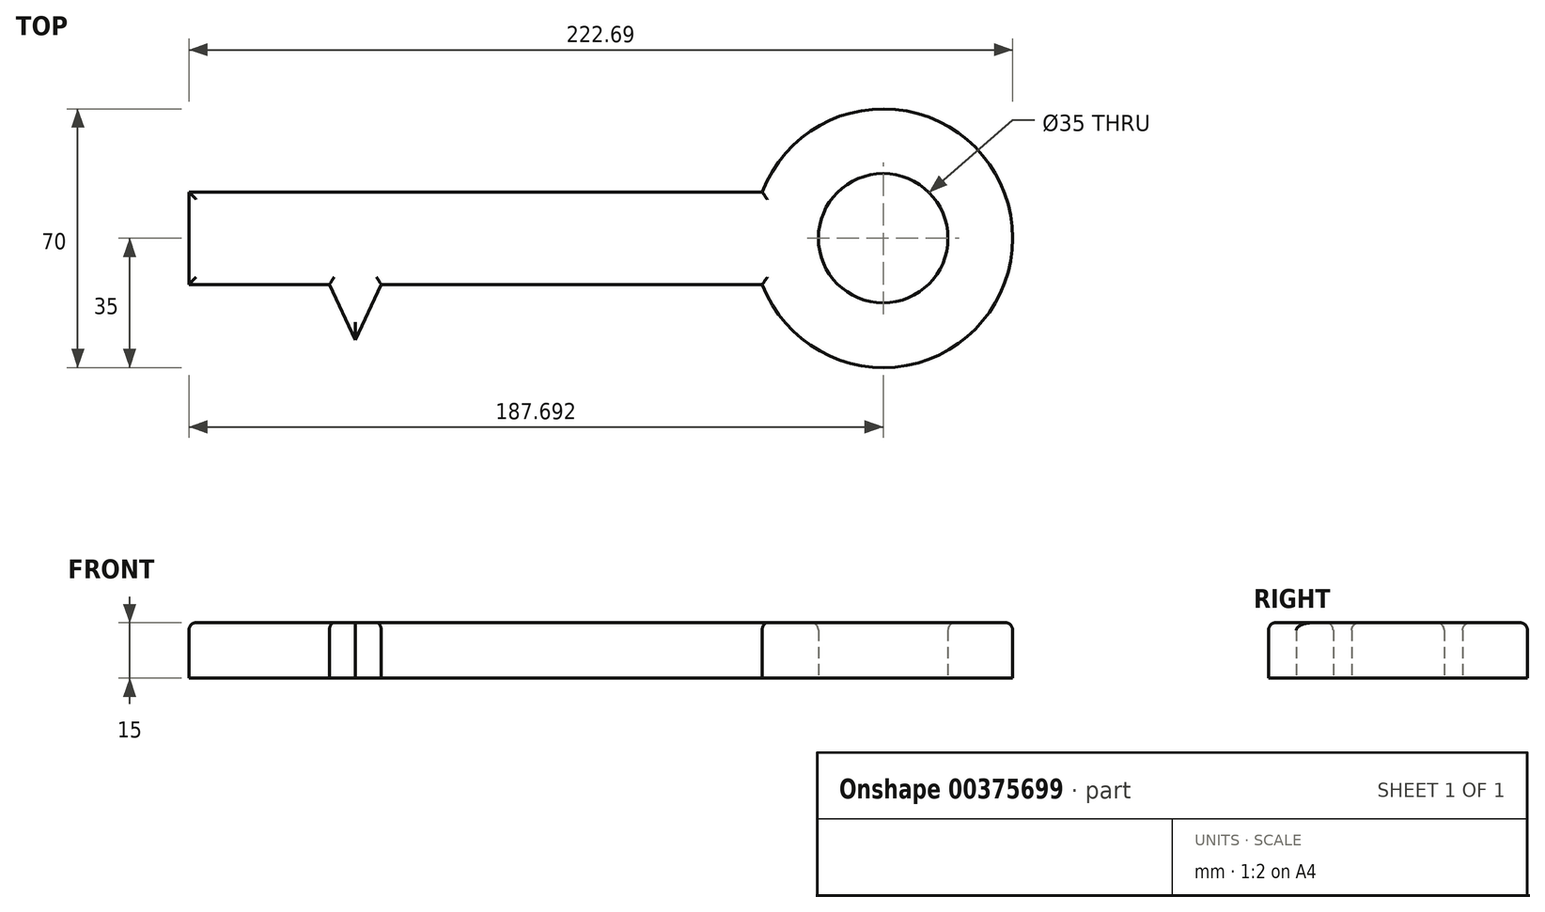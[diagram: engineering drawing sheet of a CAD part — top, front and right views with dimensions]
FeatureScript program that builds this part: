
annotation { "Feature Type Name" : "Feature", "Feature Type Description" : "" }
export const myFeature = defineFeature(function(context is Context, id is Id, definition is map)
    precondition{}
    {
        {
            var Q0;
            Q0=qCreatedBy(makeId("Top.planeOp"),FACE);
            var sketch = newSketch(context, id + "F0", { "sketchPlane" : qUnion([Q0])});
            skLineSegment(sketch, "E0.bottom", {"start": v(-45, 38.56) * mm, "end": v(110, 38.56) * mm});
            skLineSegment(sketch, "E0.top", {"start": v(-45, 13.56) * mm, "end": v(110, 13.56) * mm});
            skLineSegment(sketch, "E0.left", {"start": v(-45, 38.56) * mm, "end": v(-45, 13.56) * mm});
            skLineSegment(sketch, "E0.right", {"start": v(110, 38.56) * mm, "end": v(110, 13.56) * mm});
            skLineSegment(sketch, "E1.bottom", {"start": v(-45, 13.56) * mm, "end": v(-35, 13.56) * mm});
            skLineSegment(sketch, "E1.top", {"start": v(-45, -16.44) * mm, "end": v(-35, -16.44) * mm});
            skLineSegment(sketch, "E1.left", {"start": v(-45, 13.56) * mm, "end": v(-45, -16.44) * mm});
            skLineSegment(sketch, "E1.right", {"start": v(-35, 13.56) * mm, "end": v(-35, -16.44) * mm});
            skLineSegment(sketch, "E2.bottom", {"start": v(-25, 13.56) * mm, "end": v(-17, 13.56) * mm});
            skLineSegment(sketch, "E2.top", {"start": v(-25, -1.44) * mm, "end": v(-17, -1.44) * mm});
            skLineSegment(sketch, "E2.left", {"start": v(-25, 13.56) * mm, "end": v(-25, -1.44) * mm});
            skLineSegment(sketch, "E2.right", {"start": v(-17, 13.56) * mm, "end": v(-17, -1.44) * mm});
            skLineSegment(sketch, "E3", {"start": v(-7, 13.56) * mm, "end": v(-7, -16.44) * mm});
            skLineSegment(sketch, "E4", {"start": v(7, 13.56) * mm, "end": v(7, -16.44) * mm});
            skLineSegment(sketch, "E5", {"start": v(0, 13.56) * mm, "end": v(0, -16.44) * mm});
            skLineSegment(sketch, "E6", {"start": v(-7, 13.56) * mm, "end": v(0, -1.44) * mm});
            skLineSegment(sketch, "E7", {"start": v(7, 13.56) * mm, "end": v(0, -1.44) * mm});
            skArc(sketch, "E8", {"start": v(110, 13.56) * mm, "mid": v(177.7, 26.06) * mm, "end": v(110, 38.56) * mm});
            skCircle(sketch, "E9", {"center": v(142.7, 26.06) * mm, "radius": 17.5 * mm});
            skLineSegment(sketch, "E10", {"start": v(142.7, 26.06) * mm, "end": v(-45, 26.06) * mm, "construction": true});
            skSolve(sketch);
        }
        {
            var Q0;
            Q0=makeQuery(id+"F0.imprint","IMPRINT",FACE,{"disambiguationData":[TD([[makeQuery(id+"F0.imprint","IMPRINT",EDGE,{"derivedFrom":sQuery(id+"F0.wireOp",EDGE,"E0.bottom")}),-1.0]])]});
            var Q1;
            Q1=makeQuery(id+"F0.imprint","IMPRINT",FACE,{"disambiguationData":[TD([[makeQuery(id+"F0.imprint","IMPRINT",EDGE,{"derivedFrom":sQuery(id+"F0.wireOp",EDGE,"E2.bottom")}),-1.0]])]});
            var Q2;
            Q2=makeQuery(id+"F0.imprint","IMPRINT",FACE,{"disambiguationData":[TD([[makeQuery(id+"F0.imprint","IMPRINT",EDGE,{"derivedFrom":sQuery(id+"F0.wireOp",EDGE,"E1.bottom")}),-1.0]])]});
            var Q3;
            {var subQ0=sQuery(id+"F0.wireOp",EDGE,"E6");Q3=makeQuery(id+"F0.imprint","IMPRINT",FACE,{"disambiguationData":[TD([[makeQuery(id+"F0.imprint","IMPRINT",EDGE,{"derivedFrom":subQ0}),1.0]])]});}
            var Q4;
            {var subQ0=sQuery(id+"F0.wireOp",EDGE,"E7");Q4=makeQuery(id+"F0.imprint","IMPRINT",FACE,{"disambiguationData":[TD([[makeQuery(id+"F0.imprint","IMPRINT",EDGE,{"derivedFrom":subQ0}),-1.0]])]});}
            var Q5;
            Q5=makeQuery(id+"F0.imprint","IMPRINT",FACE,{"disambiguationData":[TD([[makeQuery(id+"F0.imprint","IMPRINT",EDGE,{"derivedFrom":sQuery(id+"F0.wireOp",EDGE,"E0.right")}),1.0]])]});
            extrude(context, id + "F1", {"entities" : qUnion([Q0, Q1, Q2, Q3, Q4, Q5]), "depth" : 15 * mm});
        }
        {
            var Q0;
            Q0=makeQuery(id+"F1.opExtrude","CAP_FACE",FACE,{"disambiguationData":[OSD([sQuery(id+"F0.wireOp",EDGE,"E0.bottom"),sQuery(id+"F0.wireOp",EDGE,"E0.top"),sQuery(id+"F0.wireOp",EDGE,"E0.left"),sQuery(id+"F0.wireOp",EDGE,"E1.top"),sQuery(id+"F0.wireOp",EDGE,"E1.left"),sQuery(id+"F0.wireOp",EDGE,"E1.right"),sQuery(id+"F0.wireOp",EDGE,"E2.top"),sQuery(id+"F0.wireOp",EDGE,"E2.left"),sQuery(id+"F0.wireOp",EDGE,"E2.right"),sQuery(id+"F0.wireOp",EDGE,"E6"),sQuery(id+"F0.wireOp",EDGE,"E7"),sQuery(id+"F0.wireOp",EDGE,"E8"),sQuery(id+"F0.wireOp",EDGE,"E9")])],"isStart":false});
            var Q1;
            Q1=makeQuery(id+"F1.opExtrude","CAP_EDGE",EDGE,{"disambiguationData":[OSD([sQuery(id+"F0.wireOp",EDGE,"E2.right")])],"isStart":false});
            var Q2;
            Q2=makeQuery(id+"F1.opExtrude","CAP_EDGE",EDGE,{"disambiguationData":[OSD([sQuery(id+"F0.wireOp",EDGE,"E0.left"),sQuery(id+"F0.wireOp",EDGE,"E1.left")])],"isStart":false});
            var Q3;
            Q3=makeQuery(id+"F1.opExtrude","CAP_EDGE",EDGE,{"disambiguationData":[OSD([sQuery(id+"F0.wireOp",EDGE,"E0.bottom")])],"isStart":false});
            var Q4;
            {var subQ0=sQuery(id+"F0.wireOp",EDGE,"E0.top");Q4=makeQuery(id+"F1.opExtrude","CAP_EDGE",EDGE,{"disambiguationData":[OSD([subQ0]),TDD([makeQuery(id+"F0.imprint","IMPRINT",EDGE,{"disambiguationData":[TD([[makeQuery(id+"F0.imprint","INTERSECT",VERTEX,{"derivedFrom":[subQ0,sQuery(id+"F0.wireOp",EDGE,"E6")]}),1.0]])],"derivedFrom":subQ0})])],"isStart":false});}
            var Q5;
            {var subQ0=sQuery(id+"F0.wireOp",EDGE,"E0.top");Q5=makeQuery(id+"F1.opExtrude","CAP_EDGE",EDGE,{"disambiguationData":[OSD([subQ0]),TDD([makeQuery(id+"F0.imprint","IMPRINT",EDGE,{"disambiguationData":[TD([[makeQuery(id+"F0.imprint","INTERSECT",VERTEX,{"derivedFrom":[subQ0,sQuery(id+"F0.wireOp",EDGE,"E1.bottom"),sQuery(id+"F0.wireOp",EDGE,"E1.right")]}),-1.0]])],"derivedFrom":subQ0})])],"isStart":false});}
            var Q6;
            Q6=makeQuery(id+"F1.opExtrude","CAP_EDGE",EDGE,{"disambiguationData":[OSD([sQuery(id+"F0.wireOp",EDGE,"E1.right")])],"isStart":false});
            var Q7;
            Q7=makeQuery(id+"F1.opExtrude","CAP_EDGE",EDGE,{"disambiguationData":[OSD([sQuery(id+"F0.wireOp",EDGE,"E2.left")])],"isStart":false});
            var Q8;
            {var subQ0=sQuery(id+"F0.wireOp",EDGE,"E0.top");Q8=makeQuery(id+"F1.opExtrude","CAP_EDGE",EDGE,{"disambiguationData":[OSD([subQ0]),TDD([makeQuery(id+"F0.imprint","IMPRINT",EDGE,{"disambiguationData":[TD([[makeQuery(id+"F0.imprint","INTERSECT",VERTEX,{"derivedFrom":[subQ0,sQuery(id+"F0.wireOp",EDGE,"E7")]}),-1.0]])],"derivedFrom":subQ0})])],"isStart":false});}
            var Q9;
            Q9=makeQuery(id+"F1.opExtrude","CAP_EDGE",EDGE,{"disambiguationData":[OSD([sQuery(id+"F0.wireOp",EDGE,"E8")])],"isStart":false});
            var Q10;
            Q10=makeQuery(id+"F1.opExtrude","CAP_EDGE",EDGE,{"disambiguationData":[OSD([sQuery(id+"F0.wireOp",EDGE,"E9")])],"isStart":false});
            fillet(context, id + "F2", {"entities" : qUnion([Q0, Q1, Q2, Q3, Q4, Q5, Q6, Q7, Q8, Q9, Q10]), "radius" : 2 * mm, "tangentPropagation" : true, "allowEdgeOverflow" : false});
        }
    });
